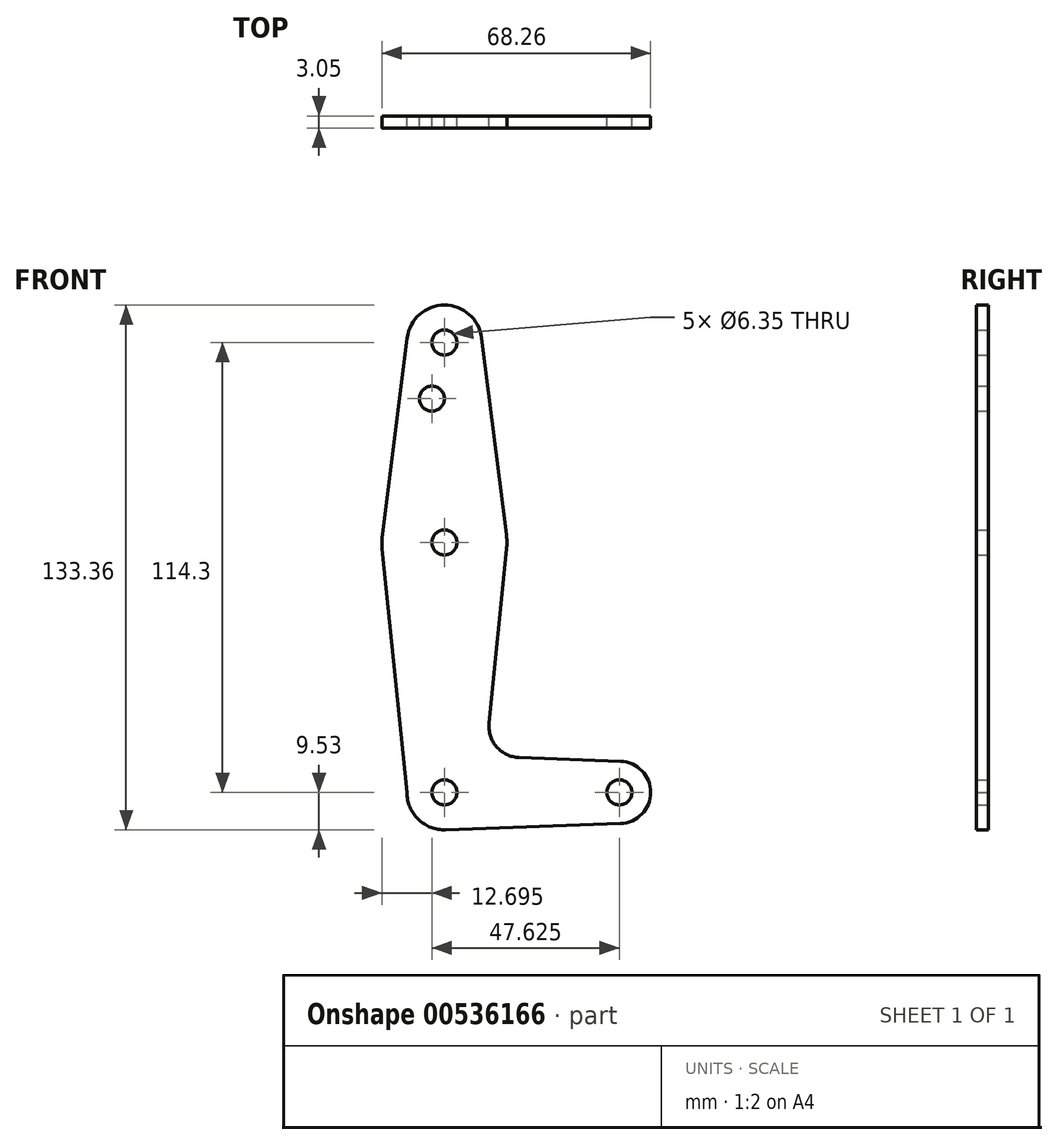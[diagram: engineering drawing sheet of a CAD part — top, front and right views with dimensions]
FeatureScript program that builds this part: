
annotation { "Feature Type Name" : "Feature", "Feature Type Description" : "" }
export const myFeature = defineFeature(function(context is Context, id is Id, definition is map)
    precondition{}
    {
        {
            var Q0;
            Q0=qCreatedBy(makeId("Front.planeOp"),FACE);
            var sketch = newSketch(context, id + "F0", { "sketchPlane" : qUnion([Q0])});
            skLineSegment(sketch, "E0", {"start": v(0, 0) * mm, "end": v(0, 114.3) * mm, "construction": true});
            skLineSegment(sketch, "E1", {"start": v(0, 0) * mm, "end": v(44.45, 0) * mm, "construction": true});
            skCircle(sketch, "E2", {"center": v(0, 0) * mm, "radius": 9.53 * mm});
            skCircle(sketch, "E3", {"center": v(0, 114.3) * mm, "radius": 9.53 * mm});
            skCircle(sketch, "E4", {"center": v(0, 63.5) * mm, "radius": 15.88 * mm});
            skCircle(sketch, "E5", {"center": v(44.45, 0) * mm, "radius": 7.94 * mm});
            skLineSegment(sketch, "E6", {"start": v(-9.53, 0) * mm, "end": v(-15.8, 61.9) * mm});
            skLineSegment(sketch, "E7", {"start": v(11.34, 17.6) * mm, "end": v(15.8, 61.9) * mm});
            skLineSegment(sketch, "E8", {"start": v(-15.75, 65.48) * mm, "end": v(-9.45, 115.5) * mm});
            skLineSegment(sketch, "E9", {"start": v(9.45, 115.5) * mm, "end": v(15.75, 65.48) * mm});
            skLineSegment(sketch, "E10", {"start": v(18.97, 8.85) * mm, "end": v(44.73, 7.93) * mm});
            skLineSegment(sketch, "E11", {"start": v(44.73, -7.93) * mm, "end": v(0, -9.53) * mm});
            skCircle(sketch, "E12", {"center": v(0, 114.3) * mm, "radius": 3.18 * mm});
            skCircle(sketch, "E13", {"center": v(0, 63.5) * mm, "radius": 3.18 * mm});
            skCircle(sketch, "E14", {"center": v(-3.18, 100.03) * mm, "radius": 3.18 * mm});
            skCircle(sketch, "E15", {"center": v(0, 0) * mm, "radius": 3.18 * mm});
            skCircle(sketch, "E16", {"center": v(44.45, 0) * mm, "radius": 3.18 * mm});
            skArc(sketch, "E17.filletArc", {"start": v(11.34, 17.6) * mm, "mid": v(13.26, 11.57) * mm, "end": v(18.97, 8.85) * mm});
            skSolve(sketch);
        }
        {
            var Q0;
            Q0 = qSketchRegion(id + "F0", true);
            extrude(context, id + "F1", {"entities" : qUnion([Q0]), "depth" : 3.05 * mm, "offsetDistance" : 25.4 * mm});
        }
    });
